# Revit family: AFX-Beverly-Outdoor_Flush_Mount-1
name_source: partatom
category: Lighting Fixtures
units: mm (PartAtom-declared; Revit-internal decimal feet)

## family parameters
Cut with Voids When Loaded = No
Host = Face
Light Source = Yes
Part Type = Normal
Room Calculation Point = No
Round Connector Dimension = Use Diameter
Shared = No

## types (1)
- BVYW0608LAJUDBK
    Apparent Load = 0 VA
    Assembly Code = D5020200
    Color Filter = 16777215
    Colour Rendering Index = 90
    Default Elevation = 48"
    Depth = 8"
    Description = LED Outdoor Flush Mount - 2 1/2" Dia x 8"D
    Diameter = 2 1/2"
    Diffuser Finish = AFX - Aluminum
    Dimming Lamp Color Temperature Shift = <None>
    Emit Shape Visible in Rendering = No
    Emit from Circle Diameter = 2"
    Housing Finish = AFX - Paint Finish Black
    Keynote = 12500
    Manufacturer = AFX Inc
    Model = BVYW0608LAJUDBK
    Photometric Web File = BVYW0608LAJUDSN_3000K_IES.IES
    Power Factor = 1
    Product Documentation Link = https://www.afxinc.com
    Revit Model Built By = https://www.servex-us.com
    Sustainability = https://lamprecycle.org
    Tilt Angle = -90.00°
    Type Comments = Beverly
    URL = https://www.afxinc.com
    Voltage = 120 V
    Wattage Comments = 9w

## geometry (parser evidence)
native form markers: Sweep x2
no freeform markers — native parametric forms only
